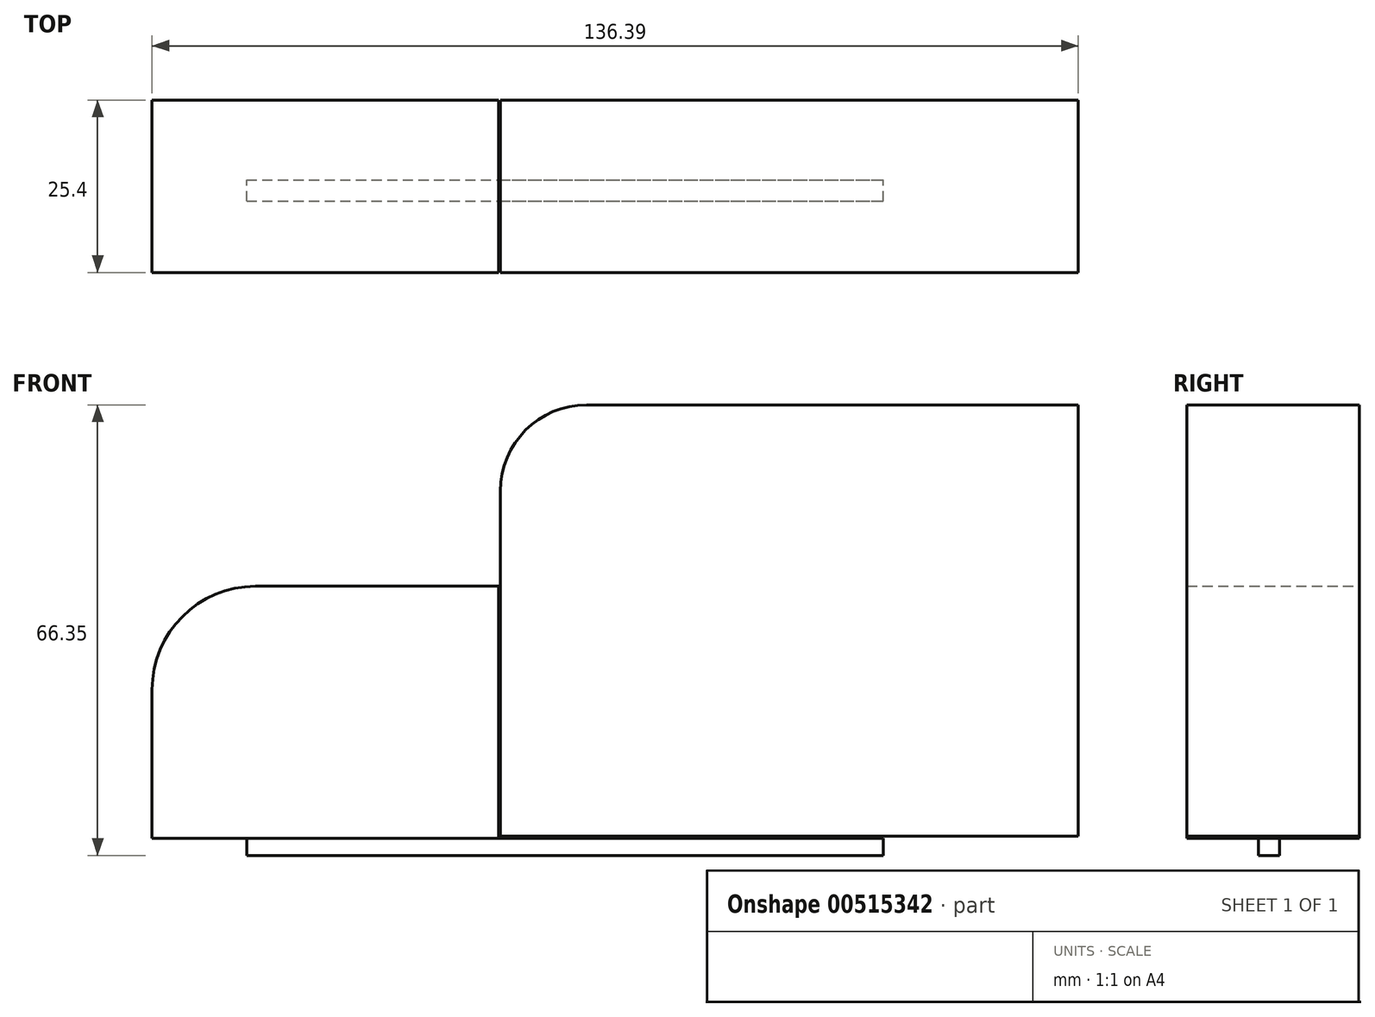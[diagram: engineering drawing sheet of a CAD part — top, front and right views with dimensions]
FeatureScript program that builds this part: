
annotation { "Feature Type Name" : "Feature", "Feature Type Description" : "" }
export const myFeature = defineFeature(function(context is Context, id is Id, definition is map)
    precondition{}
    {
        {
            var Q0;
            Q0=qCreatedBy(makeId("Front.planeOp"),FACE);
            var sketch = newSketch(context, id + "F0", { "sketchPlane" : qUnion([Q0])});
            skLineSegment(sketch, "E0.bottom", {"start": v(-7.17, 24.34) * mm, "end": v(65.24, 24.34) * mm});
            skLineSegment(sketch, "E0.top", {"start": v(-19.87, -39.2) * mm, "end": v(65.24, -39.2) * mm});
            skLineSegment(sketch, "E0.left", {"start": v(-19.87, 11.64) * mm, "end": v(-19.87, -39.2) * mm});
            skLineSegment(sketch, "E0.right", {"start": v(65.24, 24.34) * mm, "end": v(65.24, -39.2) * mm});
            skPoint(sketch, "E1.visualSharp", {"position": v(-19.87, 24.34) * mm});
            skArc(sketch, "E1.filletArc", {"start": v(-7.17, 24.34) * mm, "mid": v(-16.15, 20.62) * mm, "end": v(-19.87, 11.64) * mm});
            skSolve(sketch);
        }
        {
            var Q0;
            Q0=qCreatedBy(makeId("Front.planeOp"),FACE);
            var sketch = newSketch(context, id + "F1", { "sketchPlane" : qUnion([Q0])});
            skLineSegment(sketch, "E2.bottom", {"start": v(-20.14, -2.37) * mm, "end": v(-55.9, -2.37) * mm});
            skLineSegment(sketch, "E2.top", {"start": v(-20.14, -39.47) * mm, "end": v(-71.15, -39.47) * mm});
            skLineSegment(sketch, "E2.left", {"start": v(-20.14, -2.37) * mm, "end": v(-20.14, -39.47) * mm});
            skLineSegment(sketch, "E2.right", {"start": v(-71.15, -17.61) * mm, "end": v(-71.15, -39.47) * mm});
            skPoint(sketch, "E3.visualSharp", {"position": v(-71.15, -2.37) * mm});
            skArc(sketch, "E3.filletArc", {"start": v(-55.9, -2.37) * mm, "mid": v(-66.69, -6.84) * mm, "end": v(-71.15, -17.61) * mm});
            skSolve(sketch);
        }
        {
            var Q0;
            Q0=makeQuery(id+"F0.imprint","IMPRINT",FACE,{"disambiguationData":[TD([[makeQuery(id+"F0.imprint","IMPRINT",EDGE,{"derivedFrom":sQuery(id+"F0.wireOp",EDGE,"E0.bottom")}),-1.0]])]});
            extrude(context, id + "F2", {"entities" : qUnion([Q0]), "depth" : 25.4 * mm, "offsetDistance" : 25.4 * mm});
        }
        {
            var Q0;
            Q0=makeQuery(id+"F1.imprint","IMPRINT",FACE,{"disambiguationData":[TD([[makeQuery(id+"F1.imprint","IMPRINT",EDGE,{"derivedFrom":sQuery(id+"F1.wireOp",EDGE,"E2.bottom")}),1.0]])]});
            extrude(context, id + "F3", {"entities" : qUnion([Q0]), "depth" : 25.4 * mm, "offsetDistance" : 25.4 * mm});
        }
        {
            var Q0;
            Q0=qCreatedBy(makeId("Front.planeOp"),FACE);
            var sketch = newSketch(context, id + "F4", { "sketchPlane" : qUnion([Q0])});
            skCircle(sketch, "E4", {"center": v(-62.48, -39.47) * mm, "radius": 5.32 * mm});
            skCircle(sketch, "E5", {"center": v(43.3, -39.2) * mm, "radius": 6.34 * mm});
            skSolve(sketch);
        }
        {
            var Q0;
            Q0=sQuery(id+"F4.wireOp",EDGE,"E4");
            extrude(context, id + "F5", {"bodyType" : ToolBodyType.SURFACE, "surfaceEntities" : qUnion([Q0]), "depth" : 25.4 * mm, "offsetDistance" : 25.4 * mm});
        }
        {
            var Q0;
            Q0=sQuery(id+"F4.wireOp",EDGE,"E5");
            extrude(context, id + "F6", {"bodyType" : ToolBodyType.SURFACE, "surfaceEntities" : qUnion([Q0]), "depth" : 25.4 * mm, "offsetDistance" : 25.4 * mm});
        }
        {
            var Q0;
            Q0=makeQuery(id+"F3.opExtrude","SWEPT_FACE",FACE,{"disambiguationData":[OSD([sQuery(id+"F1.wireOp",EDGE,"E2.top")])]});
            var sketch = newSketch(context, id + "F7", { "sketchPlane" : qUnion([Q0])});
            skLineSegment(sketch, "E6.bottom", {"start": v(-57.23, 14.9) * mm, "end": v(36.5, 14.9) * mm});
            skLineSegment(sketch, "E6.top", {"start": v(-57.23, 11.74) * mm, "end": v(36.5, 11.74) * mm});
            skLineSegment(sketch, "E6.left", {"start": v(-57.23, 14.9) * mm, "end": v(-57.23, 11.74) * mm});
            skLineSegment(sketch, "E6.right", {"start": v(36.5, 14.9) * mm, "end": v(36.5, 11.74) * mm});
            skSolve(sketch);
        }
        {
            var Q0;
            {var subQ0=sQuery(id+"F7.wireOp",EDGE,"E6.left");Q0=makeQuery(id+"F7.imprint","IMPRINT",FACE,{"disambiguationData":[TD([[makeQuery(id+"F7.imprint","IMPRINT",EDGE,{"derivedFrom":subQ0}),1.0]])]});}
            var Q1;
            {var subQ0=sQuery(id+"F7.wireOp",EDGE,"E6.right");Q1=makeQuery(id+"F7.imprint","IMPRINT",FACE,{"disambiguationData":[TD([[makeQuery(id+"F7.imprint","IMPRINT",EDGE,{"derivedFrom":subQ0}),-1.0]])]});}
            extrude(context, id + "F8", {"entities" : qUnion([Q0, Q1]), "operationType" : NewBodyOperationType.ADD, "depth" : 2.54 * mm, "offsetDistance" : 25.4 * mm});
        }
    });
